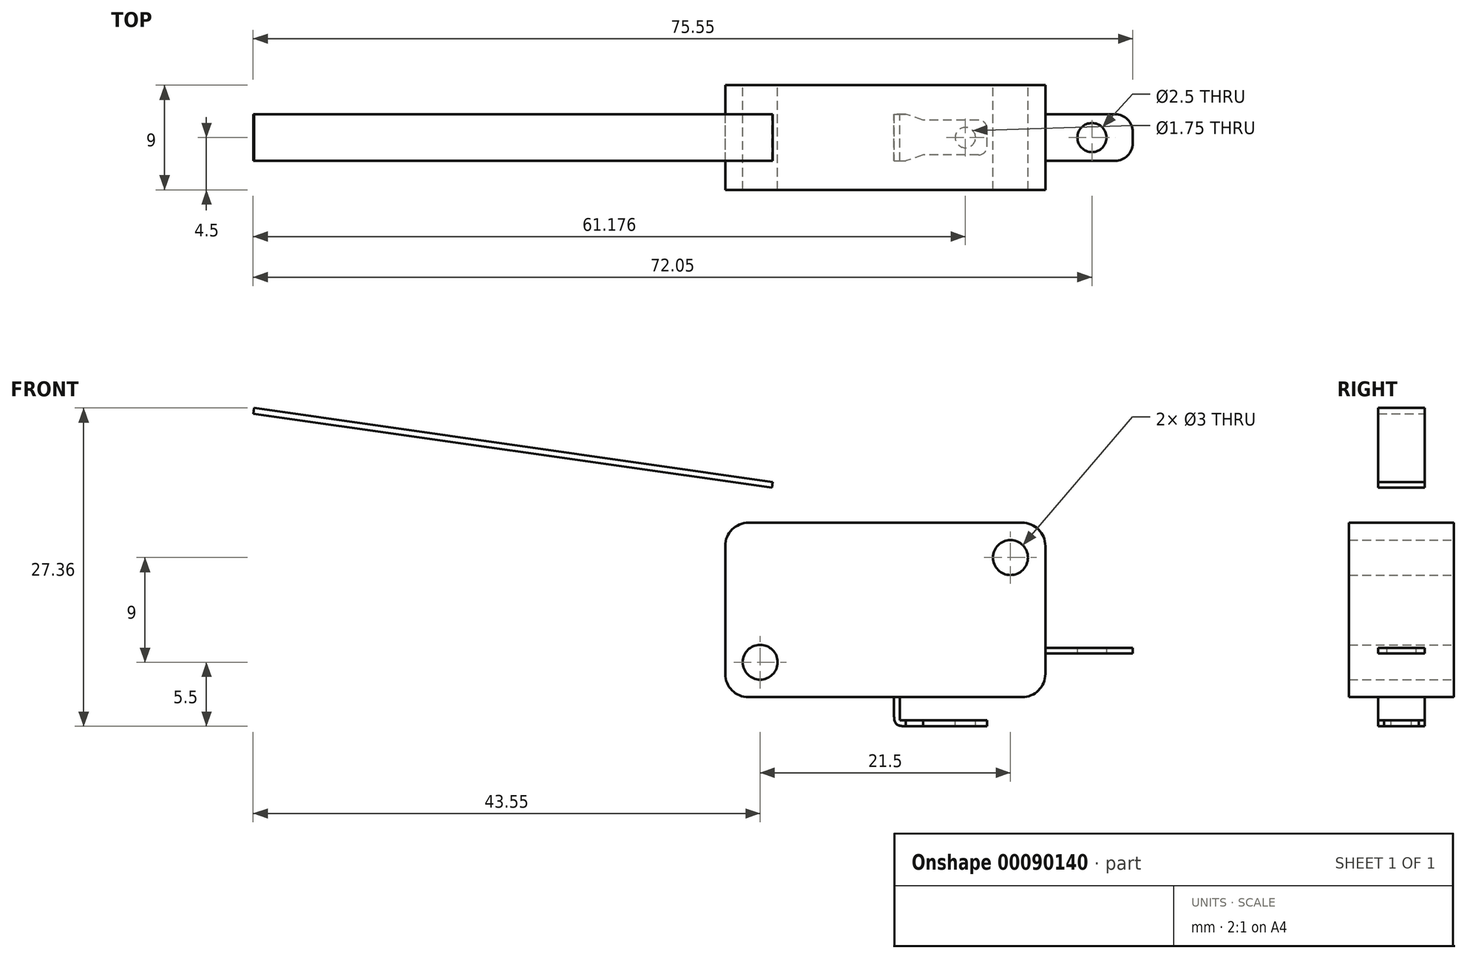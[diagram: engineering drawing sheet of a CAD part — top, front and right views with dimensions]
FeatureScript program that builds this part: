
annotation { "Feature Type Name" : "Feature", "Feature Type Description" : "" }
export const myFeature = defineFeature(function(context is Context, id is Id, definition is map)
    precondition{}
    {
        {
            var Q0;
            Q0=qCreatedBy(makeId("Front.planeOp"),FACE);
            var sketch = newSketch(context, id + "F0", { "sketchPlane" : qUnion([Q0])});
            skLineSegment(sketch, "E0.bottom", {"start": v(2, 0) * mm, "end": v(25.5, 0) * mm});
            skLineSegment(sketch, "E0.top", {"start": v(2, 15) * mm, "end": v(25.5, 15) * mm});
            skLineSegment(sketch, "E0.left", {"start": v(0, 2) * mm, "end": v(0, 13) * mm});
            skLineSegment(sketch, "E0.right", {"start": v(27.5, 2) * mm, "end": v(27.5, 13) * mm});
            skCircle(sketch, "E1", {"center": v(24.5, 12) * mm, "radius": 1.5 * mm});
            skCircle(sketch, "E2", {"center": v(3, 3) * mm, "radius": 1.5 * mm});
            skPoint(sketch, "E3.visualSharp", {"position": v(27.5, 0) * mm});
            skArc(sketch, "E3.filletArc", {"start": v(25.5, 0) * mm, "mid": v(26.91, 0.59) * mm, "end": v(27.5, 2) * mm});
            skPoint(sketch, "E4.visualSharp", {"position": v(27.5, 15) * mm});
            skArc(sketch, "E4.filletArc", {"start": v(27.5, 13) * mm, "mid": v(26.91, 14.41) * mm, "end": v(25.5, 15) * mm});
            skPoint(sketch, "E5.visualSharp", {"position": v(0, 0) * mm});
            skArc(sketch, "E5.filletArc", {"start": v(0, 2) * mm, "mid": v(0.59, 0.59) * mm, "end": v(2, 0) * mm});
            skPoint(sketch, "E6.visualSharp", {"position": v(0, 15) * mm});
            skArc(sketch, "E6.filletArc", {"start": v(2, 15) * mm, "mid": v(0.59, 14.41) * mm, "end": v(0, 13) * mm});
            skLineSegment(sketch, "E7", {"start": v(0, 15) * mm, "end": v(11, 15) * mm});
            skLineSegment(sketch, "E8.bottom", {"start": v(11, 15) * mm, "end": v(11.5, 15) * mm});
            skLineSegment(sketch, "E8.left", {"start": v(11, 15) * mm, "end": v(11, 17) * mm});
            skLineSegment(sketch, "E8.right", {"start": v(11.5, 15) * mm, "end": v(11.5, 17) * mm});
            skLineSegment(sketch, "E9", {"start": v(0, 15) * mm, "end": v(3, 15) * mm});
            skLineSegment(sketch, "E10", {"start": v(3, 15) * mm, "end": v(5, 15) * mm});
            skLineSegment(sketch, "E11.top", {"start": v(5, 17) * mm, "end": v(3, 17) * mm});
            skLineSegment(sketch, "E11.left", {"start": v(5, 15) * mm, "end": v(5, 17) * mm});
            skLineSegment(sketch, "E11.right", {"start": v(3, 15) * mm, "end": v(3, 17) * mm});
            skCircle(sketch, "E12", {"center": v(4, 17) * mm, "radius": 1 * mm});
            skLineSegment(sketch, "E13", {"start": v(4, 17) * mm, "end": v(4, 18) * mm});
            skLineSegment(sketch, "E14", {"start": v(4, 18) * mm, "end": v(11, 17) * mm});
            skLineSegment(sketch, "E15", {"start": v(4, 18) * mm, "end": v(4.07, 18.5) * mm});
            skLineSegment(sketch, "E16", {"start": v(4.07, 18.5) * mm, "end": v(11.07, 17.5) * mm});
            skLineSegment(sketch, "E17", {"start": v(11.5, 17) * mm, "end": v(11.5, 17.03) * mm});
            skLineSegment(sketch, "E18", {"start": v(11.07, 17.5) * mm, "end": v(11.5, 17.43) * mm});
            skPoint(sketch, "E19", {"position": v(11.5, 17.43) * mm});
            skPoint(sketch, "E20.third.point", {"position": v(10.66, 16.7) * mm});
            skArc(sketch, "E21.trimOffspring", {"start": v(11.5, 17) * mm, "mid": v(11.5, 17.02) * mm, "end": v(11.5, 17.03) * mm});
            skArc(sketch, "E22.trimOffspring", {"start": v(11.1, 17.5) * mm, "mid": v(11.09, 17.5) * mm, "end": v(11.07, 17.5) * mm});
            skArc(sketch, "E23", {"start": v(11.5, 17) * mm, "mid": v(11.38, 17.33) * mm, "end": v(11.07, 17.5) * mm});
            skLineSegment(sketch, "E24", {"start": v(4.07, 18.5) * mm, "end": v(-40.48, 24.86) * mm});
            skLineSegment(sketch, "E25", {"start": v(-40.48, 24.86) * mm, "end": v(-40.55, 24.36) * mm});
            skLineSegment(sketch, "E26", {"start": v(-40.55, 24.36) * mm, "end": v(4, 18) * mm});
            skSolve(sketch);
        }
        {
            var Q0;
            Q0=makeQuery(id+"F0.imprint","IMPRINT",FACE,{"disambiguationData":[TD([[makeQuery(id+"F0.imprint","IMPRINT",EDGE,{"derivedFrom":sQuery(id+"F0.wireOp",EDGE,"E0.bottom")}),1.0]])]});
            extrude(context, id + "F1", {"entities" : qUnion([Q0]), "endBound" : BoundingType.SYMMETRIC, "depth" : 9 * mm});
        }
        {
            var Q0;
            Q0=makeQuery(id+"F0.imprint","IMPRINT",FACE,{"disambiguationData":[TD([[makeQuery(id+"F0.imprint","IMPRINT",EDGE,{"derivedFrom":sQuery(id+"F0.wireOp",EDGE,"E15")}),1.0]])]});
            var Q1;
            Q1=makeQuery(id+"F0.imprint","IMPRINT",FACE,{"disambiguationData":[TD([[makeQuery(id+"F0.imprint","IMPRINT",EDGE,{"derivedFrom":sQuery(id+"F0.wireOp",EDGE,"E8.bottom")}),1.0]])]});
            extrude(context, id + "F2", {"entities" : qUnion([Q0, Q1]), "operationType" : NewBodyOperationType.ADD, "endBound" : BoundingType.SYMMETRIC, "depth" : 4 * mm});
        }
        {
            var Q0;
            {var subQ3=sQuery(id+"F0.wireOp",EDGE,"E13");Q0=makeQuery(id+"F0.imprint","IMPRINT",FACE,{"disambiguationData":[TD([[makeQuery(id+"F0.imprint","IMPRINT",EDGE,{"derivedFrom":subQ3}),1.0]])]});}
            var Q1;
            {var subQ3=sQuery(id+"F0.wireOp",EDGE,"E13");Q1=makeQuery(id+"F0.imprint","IMPRINT",FACE,{"disambiguationData":[TD([[makeQuery(id+"F0.imprint","IMPRINT",EDGE,{"derivedFrom":subQ3}),-1.0]])]});}
            var Q2;
            {var subQ1=sQuery(id+"F0.wireOp",EDGE,"E11.top");var subQ3=makeQuery(id+"F0.imprint","INTERSECT",VERTEX,{"derivedFrom":[subQ1,sQuery(id+"F0.wireOp",EDGE,"E13")]});Q2=makeQuery(id+"F0.imprint","IMPRINT",FACE,{"disambiguationData":[TD([[makeQuery(id+"F0.imprint","IMPRINT",EDGE,{"disambiguationData":[TD([[subQ3,1.0]])],"derivedFrom":subQ1}),1.0]])]});}
            var Q3;
            Q3=makeQuery(id+"F0.imprint","IMPRINT",FACE,{"disambiguationData":[TD([[makeQuery(id+"F0.imprint","IMPRINT",EDGE,{"derivedFrom":sQuery(id+"F0.wireOp",EDGE,"E10")}),1.0]])]});
            extrude(context, id + "F3", {"entities" : qUnion([Q0, Q1, Q2, Q3]), "endBound" : BoundingType.SYMMETRIC, "depth" : 3 * mm});
        }
        {
            var Q0;
            Q0=qCreatedBy(makeId("Top.planeOp"),FACE);
            cPlane(context, id + "F4", {"entities" : qUnion([Q0]), "cplaneType" : CPlaneType.OFFSET, "offset" : 3.75 * mm, "width" : 150 * mm, "height" : 150 * mm});
        }
        {
            var Q0;
            Q0=qCreatedBy(id+"F4.planeOp",FACE);
            var sketch = newSketch(context, id + "F5", { "sketchPlane" : qUnion([Q0])});
            skLineSegment(sketch, "E27.0", {"start": v(27.5, -4.5) * mm, "end": v(27.5, 4.5) * mm});
            skLineSegment(sketch, "E28.bottom", {"start": v(27.5, -2) * mm, "end": v(33.5, -2) * mm});
            skLineSegment(sketch, "E28.top", {"start": v(27.5, 2) * mm, "end": v(33.5, 2) * mm});
            skLineSegment(sketch, "E28.left", {"start": v(27.5, -2) * mm, "end": v(27.5, 2) * mm});
            skLineSegment(sketch, "E28.right", {"start": v(35, -0.5) * mm, "end": v(35, 0.5) * mm});
            skPoint(sketch, "E29.visualSharp", {"position": v(35, -2) * mm});
            skArc(sketch, "E29.filletArc", {"start": v(33.5, -2) * mm, "mid": v(34.56, -1.56) * mm, "end": v(35, -0.5) * mm});
            skPoint(sketch, "E30.visualSharp", {"position": v(35, 2) * mm});
            skArc(sketch, "E30.filletArc", {"start": v(35, 0.5) * mm, "mid": v(34.56, 1.56) * mm, "end": v(33.5, 2) * mm});
            skCircle(sketch, "E31", {"center": v(31.5, 0) * mm, "radius": 1.25 * mm});
            skPoint(sketch, "E31.centerSnap0", {"position": v(27.5, 0) * mm});
            skSolve(sketch);
        }
        {
            var Q0;
            Q0 = qSketchRegion(id + "F5", true);
            extrude(context, id + "F6", {"entities" : qUnion([Q0]), "operationType" : NewBodyOperationType.ADD, "depth" : 0.5 * mm});
        }
        {
            var Q0;
            Q0=qCreatedBy(makeId("Right.planeOp"),FACE);
            cPlane(context, id + "F7", {"entities" : qUnion([Q0]), "cplaneType" : CPlaneType.OFFSET, "offset" : 15 * mm, "width" : 150 * mm, "height" : 150 * mm});
        }
        {
            var Q0;
            Q0=qCreatedBy(id+"F7.planeOp",FACE);
            var sketch = newSketch(context, id + "F8", { "sketchPlane" : qUnion([Q0])});
            skLineSegment(sketch, "E32.0", {"start": v(-4.5, 0) * mm, "end": v(4.5, 0) * mm});
            skLineSegment(sketch, "E33.bottom", {"start": v(2, 0) * mm, "end": v(-2, 0) * mm});
            skLineSegment(sketch, "E33.top", {"start": v(2, -2) * mm, "end": v(-2, -2) * mm});
            skLineSegment(sketch, "E33.left", {"start": v(2, 0) * mm, "end": v(2, -2) * mm});
            skLineSegment(sketch, "E33.right", {"start": v(-2, 0) * mm, "end": v(-2, -2) * mm});
            skSolve(sketch);
        }
        {
            var Q0;
            Q0 = qSketchRegion(id + "F8", true);
            extrude(context, id + "F9", {"entities" : qUnion([Q0]), "operationType" : NewBodyOperationType.ADD, "oppositeDirection" : true, "depth" : 0.5 * mm});
        }
        {
            var Q0;
            Q0=makeQuery(id+"F9.opExtrude","SWEPT_FACE",FACE,{"disambiguationData":[OSD([sQuery(id+"F8.wireOp",EDGE,"E33.top")])]});
            var sketch = newSketch(context, id + "F10", { "sketchPlane" : qUnion([Q0])});
            skLineSegment(sketch, "E34.bottom", {"start": v(15, 2) * mm, "end": v(7.5, 2) * mm});
            skLineSegment(sketch, "E34.top", {"start": v(15, -2) * mm, "end": v(7.5, -2) * mm});
            skLineSegment(sketch, "E34.left", {"start": v(15, 2) * mm, "end": v(15, -2) * mm});
            skLineSegment(sketch, "E34.right", {"start": v(7.5, 2) * mm, "end": v(7.5, -2) * mm});
            skLineSegment(sketch, "E35.bottom", {"start": v(8.25, 1.5) * mm, "end": v(13, 1.5) * mm});
            skLineSegment(sketch, "E35.top", {"start": v(8.25, -1.5) * mm, "end": v(13, -1.5) * mm});
            skLineSegment(sketch, "E35.left", {"start": v(7.5, 0.75) * mm, "end": v(7.5, -0.75) * mm});
            skLineSegment(sketch, "E35.right", {"start": v(13, 1.5) * mm, "end": v(13, -1.5) * mm});
            skLineSegment(sketch, "E36", {"start": v(13, 1.5) * mm, "end": v(14.5, 2) * mm});
            skLineSegment(sketch, "E37", {"start": v(13, -1.5) * mm, "end": v(14.5, -2) * mm});
            skPoint(sketch, "E38.visualSharp", {"position": v(7.5, -1.5) * mm});
            skArc(sketch, "E38.filletArc", {"start": v(7.5, -0.75) * mm, "mid": v(7.72, -1.28) * mm, "end": v(8.25, -1.5) * mm});
            skPoint(sketch, "E39.visualSharp", {"position": v(7.5, 1.5) * mm});
            skArc(sketch, "E39.filletArc", {"start": v(8.25, 1.5) * mm, "mid": v(7.72, 1.28) * mm, "end": v(7.5, 0.75) * mm});
            skCircle(sketch, "E40", {"center": v(9.37, 0) * mm, "radius": 0.87 * mm});
            skPoint(sketch, "E40.centerSnap0", {"position": v(13, 0) * mm});
            skLineSegment(sketch, "E41.MirrorCS", {"start": v(17, 1.5) * mm, "end": v(17, -1.5) * mm});
            skLineSegment(sketch, "E42.MirrorCS", {"start": v(17, -1.5) * mm, "end": v(15.5, -2) * mm});
            skLineSegment(sketch, "E43.MirrorCS", {"start": v(17, 1.5) * mm, "end": v(15.5, 2) * mm});
            skLineSegment(sketch, "E44.MirrorCS", {"start": v(15, -2) * mm, "end": v(22.5, -2) * mm});
            skLineSegment(sketch, "E45.MirrorCS", {"start": v(15, 2) * mm, "end": v(22.5, 2) * mm});
            skLineSegment(sketch, "E46.MirrorCS", {"start": v(21.75, 1.5) * mm, "end": v(17, 1.5) * mm});
            skLineSegment(sketch, "E47.MirrorCS", {"start": v(21.75, -1.5) * mm, "end": v(17, -1.5) * mm});
            skCircle(sketch, "E48.MirrorC", {"center": v(20.63, 0) * mm, "radius": 0.87 * mm});
            skLineSegment(sketch, "E49.MirrorCS", {"start": v(22.5, 0.75) * mm, "end": v(22.5, -0.75) * mm});
            skArc(sketch, "E50.MirrorCS", {"start": v(21.75, 1.5) * mm, "mid": v(22.28, 1.28) * mm, "end": v(22.5, 0.75) * mm});
            skArc(sketch, "E51.MirrorCS", {"start": v(22.5, -0.75) * mm, "mid": v(22.28, -1.28) * mm, "end": v(21.75, -1.5) * mm});
            skLineSegment(sketch, "E52.MirrorCS", {"start": v(22.5, 2) * mm, "end": v(22.5, -2) * mm});
            skSolve(sketch);
        }
        {
            var Q0;
            {var subQ2=sQuery(id+"F10.wireOp",EDGE,"E34.left");Q0=makeQuery(id+"F10.imprint","IMPRINT",FACE,{"disambiguationData":[TD([[makeQuery(id+"F10.imprint","IMPRINT",EDGE,{"derivedFrom":subQ2}),-1.0]])]});}
            var Q1;
            Q1=makeQuery(id+"F10.imprint","IMPRINT",FACE,{"disambiguationData":[TD([[makeQuery(id+"F10.imprint","IMPRINT",EDGE,{"derivedFrom":sQuery(id+"F10.wireOp",EDGE,"E41.MirrorCS")}),1.0]])]});
            var Q2;
            {var subQ0=sQuery(id+"F10.wireOp",EDGE,"E34.left");Q2=makeQuery(id+"F10.imprint","IMPRINT",FACE,{"disambiguationData":[TD([[makeQuery(id+"F10.imprint","IMPRINT",EDGE,{"derivedFrom":subQ0}),1.0]])]});}
            extrude(context, id + "F11", {"entities" : qUnion([Q0, Q1, Q2]), "operationType" : NewBodyOperationType.ADD, "depth" : 0.5 * mm});
        }
        {
            var Q0;
            Q0=makeQuery(id+"F11.opExtrude","CAP_EDGE",EDGE,{"disambiguationData":[OSD([sQuery(id+"F8.wireOp",EDGE,"E33.top")])],"isStart":false});
            var Q1;
            Q1=makeQuery(id+"F9.opExtrude","CAP_EDGE",EDGE,{"disambiguationData":[OSD([sQuery(id+"F8.wireOp",EDGE,"E33.top")])],"isStart":true});
            fillet(context, id + "F12", {"entities" : qUnion([Q0, Q1]), "radius" : 1 * mm, "rho" : .6, "crossSection" : FilletCrossSection.CONIC, "allowEdgeOverflow" : false});
        }
        {
            var Q0;
            Q0=makeQuery(id+"F3.opExtrude","SWEPT_BODY",BODY,{"disambiguationData":[OSD([sQuery(id+"F0.wireOp",EDGE,"E10"),sQuery(id+"F0.wireOp",EDGE,"E11.left"),sQuery(id+"F0.wireOp",EDGE,"E11.right"),sQuery(id+"F0.wireOp",EDGE,"E12"),sQuery(id+"F0.wireOp",EDGE,"E14")])]});
            deleteBodies(context, id + "F13", {"entities" : qUnion([Q0])});
        }
    });
